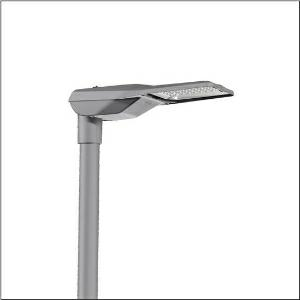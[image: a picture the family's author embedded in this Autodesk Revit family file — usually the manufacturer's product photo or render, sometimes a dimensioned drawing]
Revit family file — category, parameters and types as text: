
# Revit family: streetlight_sl_21_mini___st0_5a_5xe2b33s08hb_7adc
name_source: partatom
category: Lighting Fixtures
units: mm (PartAtom-declared; Revit-internal decimal feet)

## family parameters
Cut with Voids When Loaded = No
Host = Face
Light Source = No
Part Type = Normal
Room Calculation Point = No
Round Connector Dimension = Use Diameter
Shared = No

## types (1)
- --- (1 x LED, 9040 lm, 66 W, 3000K)
    Apparent Load = 66 VA
    CIE Flux Codes = 41 75 97 100 100
    Color Rendering = 70
    Color Temperature = 3000K
    Default Elevation = 1800 mm
    Description = Streetlight SL 21 mini, mast luminaire, primary light control with lens, of PMMA, primary optical cover: cover, of toughened safety glass, transparent, light distribution: ST0.5a, light emission: direct distribution, primary light characteristic: asymmetric, installation type: side-entry, post-top, LED, High Power LED, rated luminous flux: 9.040lm, luminous efficacy: 137lm/W, light colour: 730, colour temperature: 3000K, control gear: D4i, control: overheat protection, constant luminous flux control, time-dependent luminous flux control, flexible luminous flux parameterisation, pre-setting: logarithmic dimming characteristic, mains connection: 220..240V, AC, 50/60Hz, start of lifetime: 66W, end of service life: 69W, reduction: 30W, luminaire housing, of diecast aluminium, powder-coated, SITECO metallic grey (DB 702S), corrosivity category C5 high according to DIN EN ISO 12944, please order mast flange separately, inclination adjustable: 0°, 5°, 10°, 15°, sealing non-destructively replaceable, multi-level sealing system, length: 628mm, width: 235mm, height: 110mm, mast flange for spigot size: 42mm (side-entry): 5XC10008XM4, 60/48mm (side-entry/post-top): 5XC10108XM2, 76/60mm (side-entry/post-top): 5XC10108XM1, mounting height: 4..8m, Smart Interface above, protection rating (complete): IP66, insulation class (complete): insulation class II (safety insulation), certification: CE, ENEC, ENEC+, VDE, impact resistance: IK10, permissible operating ambient temperature for outdoor applications: -40..+50°C, standard-compliant lighting for roads and squares, packaging unit: 1 piece

Light Distribution: ST0.5a
    Height = 110 mm
    Lamp = 1 x LED
    Lamp Light Flux = 9040 lm
    Lamp Power = 66 W
    Lamp count = 1
    Length = 625 mm
    Luminous efficacy = 137 lm/W
    Manufacturer = Siteco
    ModVariant = No
    Model = 5XE2B33S08HB
    Number of Poles = 1
    OnlyDefault = Yes
    Power Factor = 1
    Product Name = Streetlight SL 21 mini | ST0.5a
    Product group = mast luminaire | pylon top
    ProductGroupID = 6100
    Protection Class = Protection class II
    Protection Degree = IP 66
    RLX_Detail_Level = 1
    RLX_Emergency_Light_Flux = 0 lm
    RLX_Emergency_Type = 0
    RLX_Emergency_Type_DB = No
    RlxData = <blob elided: 37149 chars, md5=b121b3d1>
    Socket = socket
    Standby Power = 0 W
    System Light Flux = 9040 lm
    System Power = 66 W
    Type Comments = factory setting: luminous flux: 100 % | dim-lin: 254 | 670 mA
    Type Image = l_1003515.jpg
    URL = http://relux.com
    VarID = @adj_188651
    Voltage = 0 V
    Weight = 0.00 kg
    Width = 234 mm

## geometry (parser evidence)
native form markers: Blend x4, Sweep x12
no freeform markers — native parametric forms only
